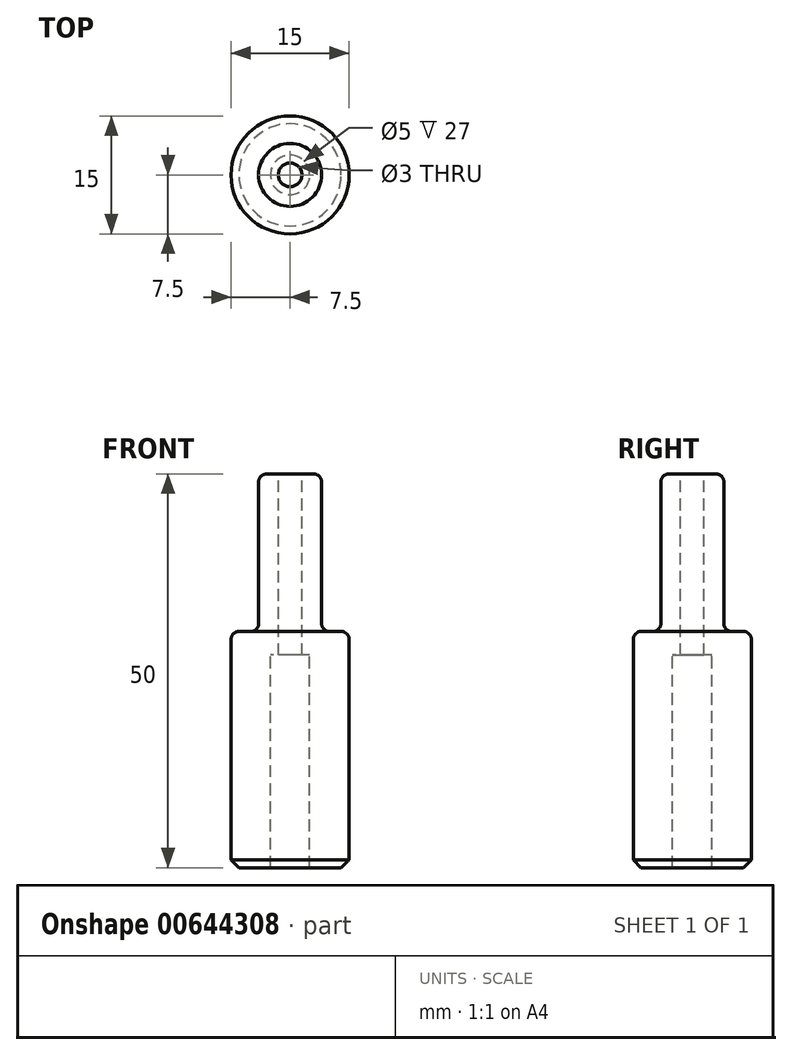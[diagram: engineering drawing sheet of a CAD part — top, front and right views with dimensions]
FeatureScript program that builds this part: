
annotation { "Feature Type Name" : "Feature", "Feature Type Description" : "" }
export const myFeature = defineFeature(function(context is Context, id is Id, definition is map)
    precondition{}
    {
        {
            var Q0;
            Q0=qCreatedBy(makeId("Right.planeOp"),FACE);
            var sketch = newSketch(context, id + "F0", { "sketchPlane" : qUnion([Q0])});
            skLineSegment(sketch, "E0", {"start": v(2.5, 0) * mm, "end": v(7.5, 0) * mm});
            skLineSegment(sketch, "E1", {"start": v(7.5, 0) * mm, "end": v(7.5, 30) * mm});
            skLineSegment(sketch, "E2", {"start": v(7.5, 30) * mm, "end": v(4, 30) * mm});
            skLineSegment(sketch, "E3", {"start": v(4, 30) * mm, "end": v(4, 50) * mm});
            skLineSegment(sketch, "E4", {"start": v(4, 50) * mm, "end": v(1.5, 50) * mm});
            skLineSegment(sketch, "E5", {"start": v(0, 44.74) * mm, "end": v(0, -19.14) * mm, "construction": true});
            skLineSegment(sketch, "E6", {"start": v(2.5, 0) * mm, "end": v(2.5, 27) * mm});
            skLineSegment(sketch, "E7", {"start": v(2.5, 27) * mm, "end": v(1.5, 27) * mm});
            skLineSegment(sketch, "E8", {"start": v(1.5, 27) * mm, "end": v(1.5, 50) * mm});
            skPoint(sketch, "E9.orphan", {"position": v(0, 50) * mm});
            skSolve(sketch);
        }
        {
            var Q0;
            Q0 = qSketchRegion(id + "F0", true);
            var Q1;
            Q1=sQuery(id+"F0.wireOp",EDGE,"E5");
            revolve(context, id + "F1", {"entities" : qUnion([Q0]), "axis" : qUnion([Q1]), "revolveType" : RevolveType.FULL});
        }
        {
            var Q0;
            Q0=makeQuery(id+"F1.opRevolve","SWEPT_EDGE",EDGE,{"disambiguationData":[OSD([sQuery(id+"F0.wireOp",EDGE,"E3"),sQuery(id+"F0.wireOp",EDGE,"E4")])]});
            var Q1;
            Q1=makeQuery(id+"F1.opRevolve","SWEPT_EDGE",EDGE,{"disambiguationData":[OSD([sQuery(id+"F0.wireOp",EDGE,"E2"),sQuery(id+"F0.wireOp",EDGE,"E3")])]});
            var Q2;
            Q2=makeQuery(id+"F1.opRevolve","SWEPT_EDGE",EDGE,{"disambiguationData":[OSD([sQuery(id+"F0.wireOp",EDGE,"E1"),sQuery(id+"F0.wireOp",EDGE,"E2")])]});
            fillet(context, id + "F2", {"entities" : qUnion([Q0, Q1, Q2]), "radius" : 1 * mm, "tangentPropagation" : true, "allowEdgeOverflow" : false});
        }
        {
            var Q0;
            Q0=makeQuery(id+"F1.opRevolve","SWEPT_EDGE",EDGE,{"disambiguationData":[OSD([sQuery(id+"F0.wireOp",EDGE,"E0"),sQuery(id+"F0.wireOp",EDGE,"E1")])]});
            chamfer(context, id + "F3", {"entities" : qUnion([Q0]), "width" : 1 * mm, "tangentPropagation" : true});
        }
    });
